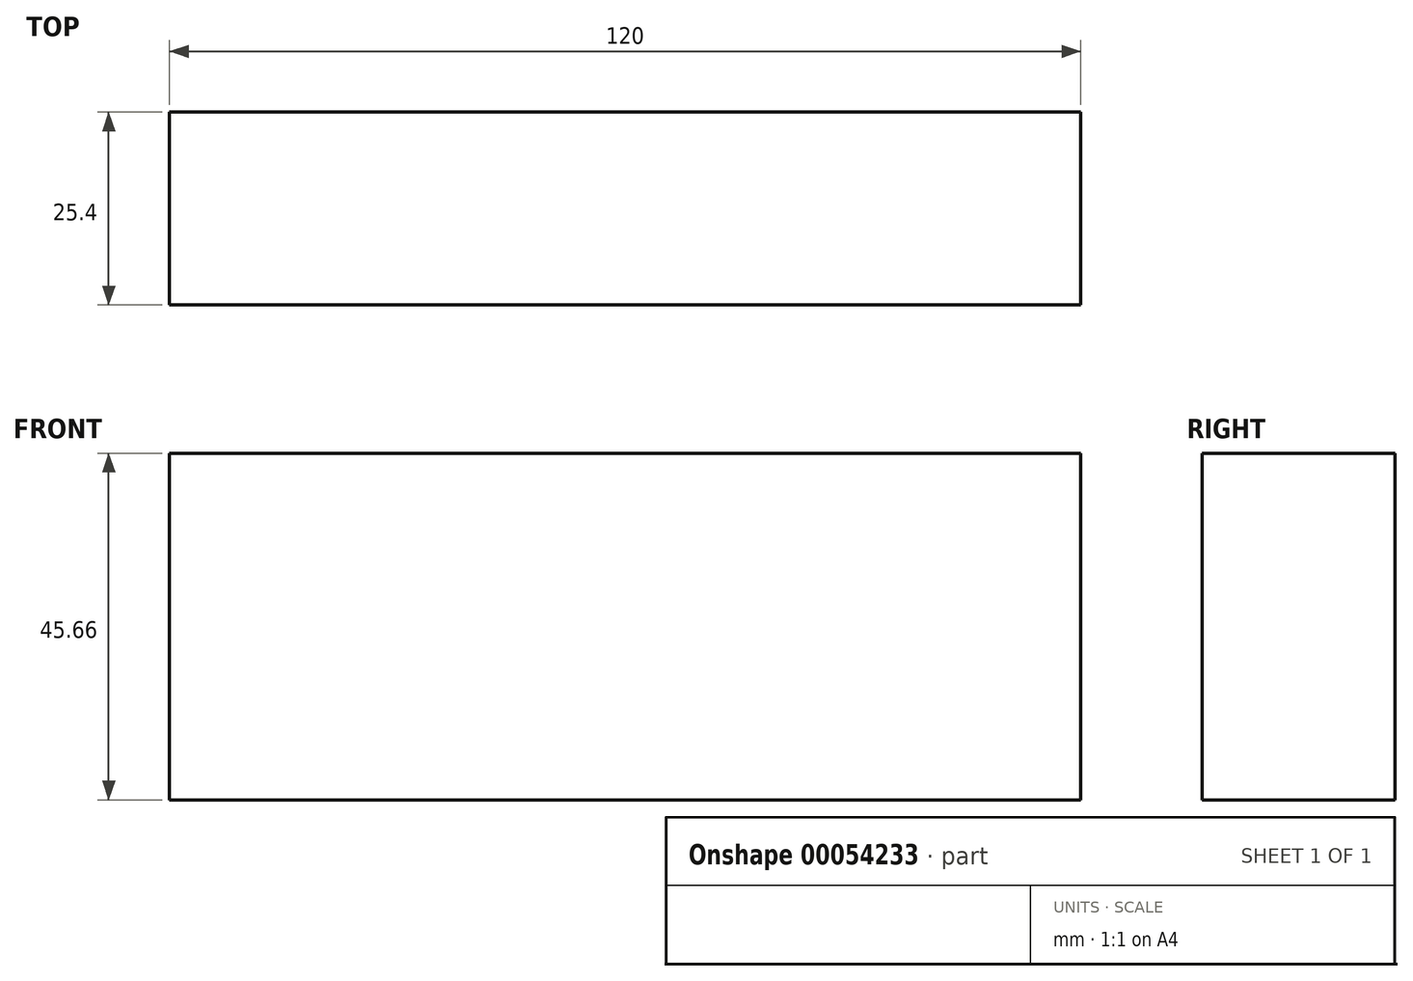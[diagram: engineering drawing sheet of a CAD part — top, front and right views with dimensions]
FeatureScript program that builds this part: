
annotation { "Feature Type Name" : "Feature", "Feature Type Description" : "" }
export const myFeature = defineFeature(function(context is Context, id is Id, definition is map)
    precondition{}
    {
        {
            var Q0;
            Q0=qCreatedBy(makeId("Front.planeOp"),FACE);
            var sketch = newSketch(context, id + "F0", { "sketchPlane" : qUnion([Q0])});
            skLineSegment(sketch, "E0.bottom", {"start": v(-58.4, 0) * mm, "end": v(61.6, 0) * mm});
            skLineSegment(sketch, "E0.top", {"start": v(-58.4, 45.66) * mm, "end": v(61.6, 45.66) * mm});
            skLineSegment(sketch, "E0.left", {"start": v(-58.4, 0) * mm, "end": v(-58.4, 45.66) * mm});
            skLineSegment(sketch, "E0.right", {"start": v(61.6, 0) * mm, "end": v(61.6, 45.66) * mm});
            skSolve(sketch);
        }
        {
            var Q0;
            Q0=makeQuery(id+"F0.imprint","IMPRINT",FACE,{"disambiguationData":[TD([[makeQuery(id+"F0.imprint","IMPRINT",EDGE,{"derivedFrom":sQuery(id+"F0.wireOp",EDGE,"E0.bottom")}),1.0]])]});
            extrude(context, id + "F1", {"entities" : qUnion([Q0]), "endBound" : BoundingType.SYMMETRIC, "depth" : 25.4 * mm});
        }
    });
